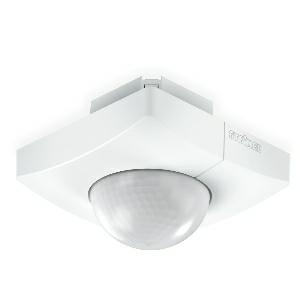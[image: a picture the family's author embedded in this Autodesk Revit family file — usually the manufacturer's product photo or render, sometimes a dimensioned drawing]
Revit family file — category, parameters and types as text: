
# Revit family: is_345_033835
name_source: partatom
category: Elektroinstallationen
revit_build: Autodesk Revit 2016 (Build: 20190508_0715(x64)
units: mm (PartAtom-declared; Revit-internal decimal feet)

## family parameters
Basisbauteil = Fläche
Beim Laden mit Abzugskörper schneiden = Nein
Bemaßung runder Anschluss = Durchmesser verwenden
Beschriftungsausrichtung beibehalten = Nein
Gemeinsam genutzt = Nein
Raumberechnungspunkt = Nein
Teiletyp = Normal

## types (1)
- IS 345
    Apparent Load = 0 VA
    Beschreibung = Type: Motion detectors; Dimensions (L x W x H): 78 x 94 x 94 mm; Mains power supply: 220 – 240 V / 50 – 60 Hz; Sensor Technology: passive infrared; Application, place: Indoors; Application, room: corridor / aisle, multi-storey / underground car park, Indoors; Installation site: ceiling; Installation: Concealed wiring; Switching zones: 280 switching zones; Electronic scalability: No; Mechanical scalability: No; Mounting height: 2,50 – 5,00 m; Optimum mounting height: 2,8 m; Detection angle: 360 °; Angle of aperture: 45 °; Sneak-by guard: Yes; Capability of masking out individual segments: Yes; Reach, radial: 12 x 6 m (72 m²); Reach, tangential: 23 x 6 m (138 m²); Twilight setting TEACH: Yes; Twilight setting: 2 – 1000 lx; Time setting: 5 sec – 15 min; Constant-lighting control: No; Basic light level function: No; Functions: Normal / test mode, Manual ON / ON-OFF; Settings via: Remote control, Potentiometers, Smart Remote; With remote control: No; Interconnection: Yes; IP-rating: IP20; Material: Plastic; Ambient temperature: -20 – 50 °C; Colour: white; Colour, RAL: 9003; Manufacturer's Warranty: 5 years; Version: PF - concealed, sq.; PU1, EAN: 4007841033835
    Height = 0 mm  [stored 0 ft]
    Hersteller = Steinel
    Length = 78 mm  [stored 0.255906 ft]
    Maximum range = 11.589 m
    ModVariant = Nein
    Modell = 033835
    Mounting Place = Ceiling
    Mounting Type = Recessed
    Number of Poles = 1
    OnlyDefault = Ja
    Power Factor = 1
    Product Name = IS 345
    Product group = Presence detector
    ProductGroupID = 4
    Protection Class = Protection class
    Protection Degree = IP 20
    RlxData = <blob elided: 137145 chars, md5=9d7865ed>
    Sensor characteristics = Stretched
    Sensor type = Passive (infrared)
    SensorDataFile = <blob elided: 5885 chars, md5=98bccc25>
    Type of entry = Motion
    Typenbild = produkt1_033835.jpg
    Typenkommentare = Product without accessories
    URL = http://relux.com
    VarID = ---
    Voltage = 0 V
    Vorgabe-Ansicht = 1800 mm
    Weight = 0.00 kg
    Width = 94 mm  [stored 0.308399 ft]

note: [stored X ft] marks values corroborated as IEEE doubles in the binary element streams (Revit-internal decimal feet)

## geometry (parser evidence)
native form markers: Sweep x18
no freeform markers — native parametric forms only
